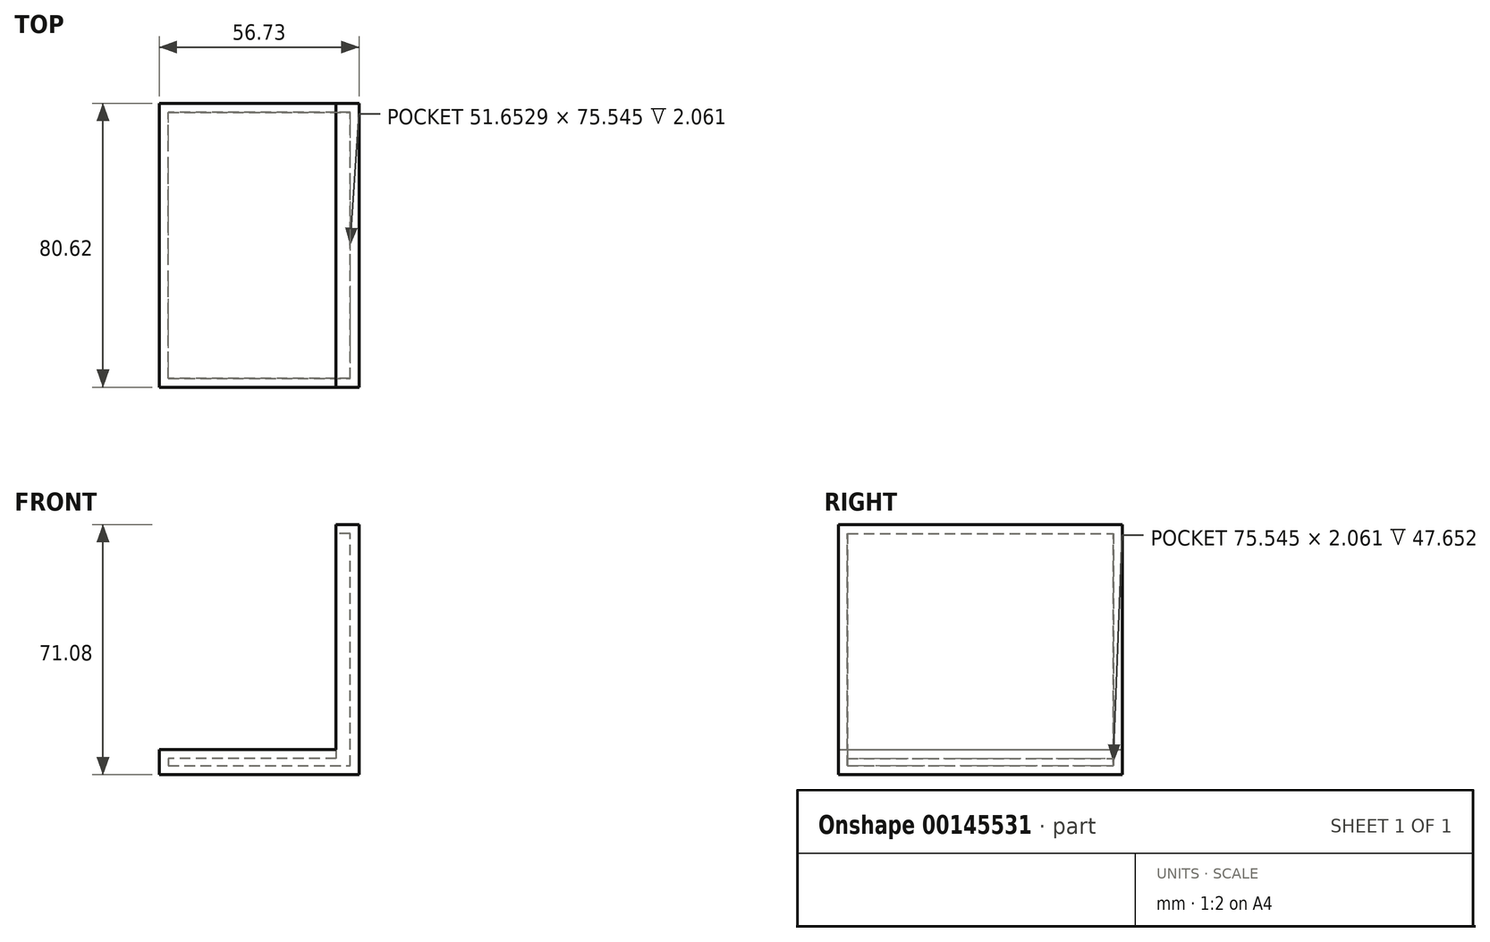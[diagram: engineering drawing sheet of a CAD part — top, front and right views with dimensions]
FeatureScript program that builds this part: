
annotation { "Feature Type Name" : "Feature", "Feature Type Description" : "" }
export const myFeature = defineFeature(function(context is Context, id is Id, definition is map)
    precondition{}
    {
        {
            var Q0;
            Q0=qCreatedBy(makeId("Front.planeOp"),FACE);
            var sketch = newSketch(context, id + "F0", { "sketchPlane" : qUnion([Q0])});
            skLineSegment(sketch, "E0", {"start": v(0, 0) * mm, "end": v(56.73, 0) * mm});
            skLineSegment(sketch, "E1", {"start": v(56.73, 0) * mm, "end": v(56.73, 71.08) * mm});
            skLineSegment(sketch, "E2", {"start": v(56.73, 71.08) * mm, "end": v(50.2, 71.08) * mm});
            skLineSegment(sketch, "E3", {"start": v(50.2, 71.08) * mm, "end": v(50.2, 7.14) * mm});
            skLineSegment(sketch, "E4", {"start": v(50.2, 7.14) * mm, "end": v(0, 7.14) * mm});
            skLineSegment(sketch, "E5", {"start": v(0, 7.14) * mm, "end": v(0, 0) * mm});
            skSolve(sketch);
        }
        {
            var Q0;
            Q0=makeQuery(id+"F0.imprint","IMPRINT",FACE,{"disambiguationData":[TD([[makeQuery(id+"F0.imprint","IMPRINT",EDGE,{"derivedFrom":sQuery(id+"F0.wireOp",EDGE,"E0")}),1.0]])]});
            extrude(context, id + "F1", {"entities" : qUnion([Q0]), "depth" : 80.62 * mm});
        }
        {
            var Q0;
            Q0=makeQuery(id+"F1.opExtrude","SWEPT_FACE",FACE,{"disambiguationData":[OSD([sQuery(id+"F0.wireOp",EDGE,"E3")])]});
            shell(context, id + "F2", {"entities" : qUnion([Q0]), "thickness" : 2.54 * mm});
        }
    });
